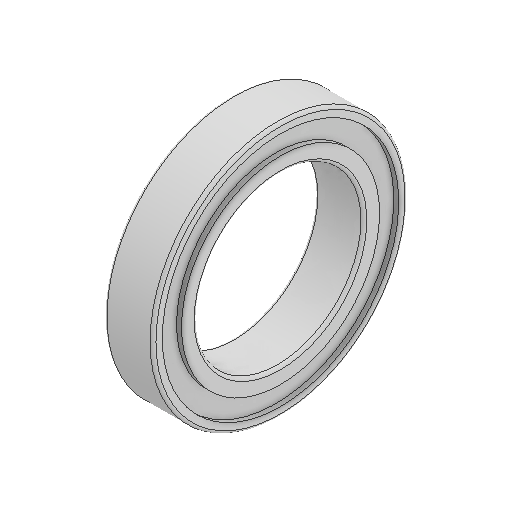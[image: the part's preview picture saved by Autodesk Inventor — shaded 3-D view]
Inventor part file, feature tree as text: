
AUTODESK INVENTOR PART (.ipt)
format: ipt  version: 2024.1 (Build 281209000, 209)  size: 165,376 bytes
history: native  units: in
note: dims shown in document units (in); Inventor stores cm internally (conversion verified against a paired STEP export)
features: fillet x1
ambient origin geometry x8: Origin, YZ Plane, XZ Plane, XY Plane, X Axis, Y Axis, Z Axis, Center Point
bodies: Solid1 (feature_tree)
feature tree (1):
  fillet  "Fillet1"  [1 undecoded]
note: 1 required parameter value undecoded (feature->parameter linkage not recoverable at this tier; creation-order binding heuristic only, values carry confidence <= 0.55)
